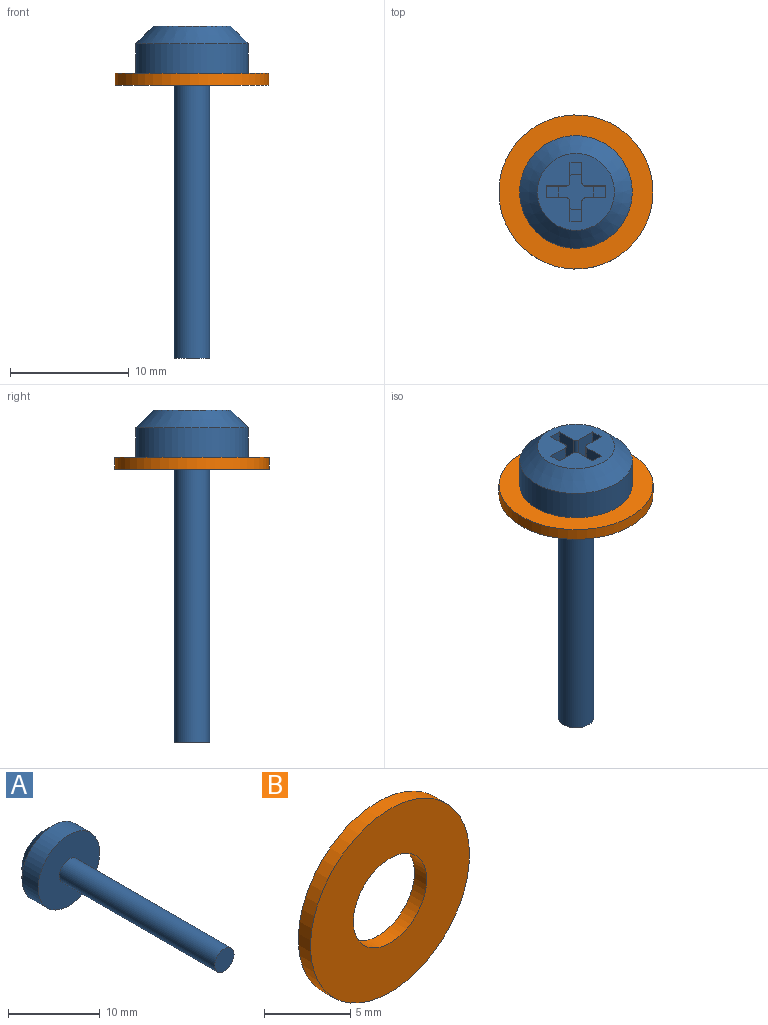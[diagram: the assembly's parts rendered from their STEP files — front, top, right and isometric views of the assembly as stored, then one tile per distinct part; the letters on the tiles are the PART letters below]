
ASSEMBLY  parts=2 mates=1
PART A: 23 faces, bbox 9.5x28x9.5 mm
  f0: plane 6.5x6.5mm, normal (0,1,0), area 24.1mm2, adj f5,f6,f7,f8,f9,f10,f11,f12
  f1: cylinder r=1.5mm len=24mm, axis (0,1,0), area 226.2mm2, adj f2,f4
  f2: plane 3x3mm, normal (0,-1,0), area 7.1mm2, adj f1
  f3: cylinder r=4.75mm len=9.5mm, axis (0,-1,0), area 74.6mm2, adj f4,f5
  f4: plane 9.5x9.5mm, normal (0,-1,0), area 63.8mm2, adj f1,f3
  f5: cone r=3.25mm half-angle=45deg, axis (0,-1,0), area 53.3mm2, adj f0,f3
  f6: plane 3.9x1.7mm, normal (1,0,0), area 6.6mm2, adj f0,f17,f18,f19
  f7: plane 3.9x1.7mm, normal (0,0,1), area 6.6mm2, adj f0,f8,f18,f19
  f8: plane 3.9x1mm, normal (1,0,0), area 3.9mm2, adj f0,f7,f9,f18
  f9: plane 3.9x1.7mm, normal (0,0,-1), area 6.6mm2, adj f0,f8,f18,f22
  f10: plane 3.9x1.7mm, normal (1,0,0), area 6.6mm2, adj f0,f11,f18,f22
  f11: plane 3.9x1mm, normal (0,0,-1), area 3.9mm2, adj f0,f10,f12,f18
  f12: plane 3.9x1.7mm, normal (-1,0,0), area 6.6mm2, adj f0,f11,f18,f21
  f13: plane 3.9x1.7mm, normal (0,0,-1), area 6.6mm2, adj f0,f14,f18,f21
  f14: plane 3.9x1mm, normal (-1,0,0), area 3.9mm2, adj f0,f13,f15,f18
  f15: plane 3.9x1.7mm, normal (0,0,1), area 6.6mm2, adj f0,f14,f18,f20
  f16: plane 3.9x1.7mm, normal (-1,0,0), area 6.6mm2, adj f0,f17,f18,f20
  f17: plane 3.9x1mm, normal (0,0,1), area 3.9mm2, adj f0,f6,f16,f18
  f18: plane 5x5mm, normal (0,1,0), area 9.1mm2, adj f6,f7,f8,f9,f10,f11,f12,f13
  f19: cylinder r=0.3mm len=3.9mm, axis (0,-1,0), area 1.8mm2, adj f0,f6,f7,f18
  f20: cylinder r=0.3mm len=3.9mm, axis (0,1,0), area 1.8mm2, adj f0,f15,f16,f18
  f21: cylinder r=0.3mm len=3.9mm, axis (0,-1,0), area 1.8mm2, adj f0,f12,f13,f18
  f22: cylinder r=0.3mm len=3.9mm, axis (0,1,0), area 1.8mm2, adj f0,f9,f10,f18
PART B: 4 faces, bbox 13x1x13 mm
  f0: cylinder r=3mm len=6mm, axis (0,1,0), area 18.8mm2, adj f2,f3
  f1: cylinder r=6.5mm len=13mm, axis (0,1,0), area 40.8mm2, adj f2,f3
  f2: plane 13x13mm, normal (0,-1,0), area 104.5mm2, adj f0,f1
  f3: plane 13x13mm, normal (0,1,0), area 104.5mm2, adj f0,f1
PLACE A rot(axis=(1,0,0),90deg) t=(0,0,0)mm
PLACE B rot(axis=(-1,0,0),90deg) t=(0,0,11.5)mm
MATE fastened B.f0 <-> A.f1  axis (0,0,1) through (0,0,12)mm
